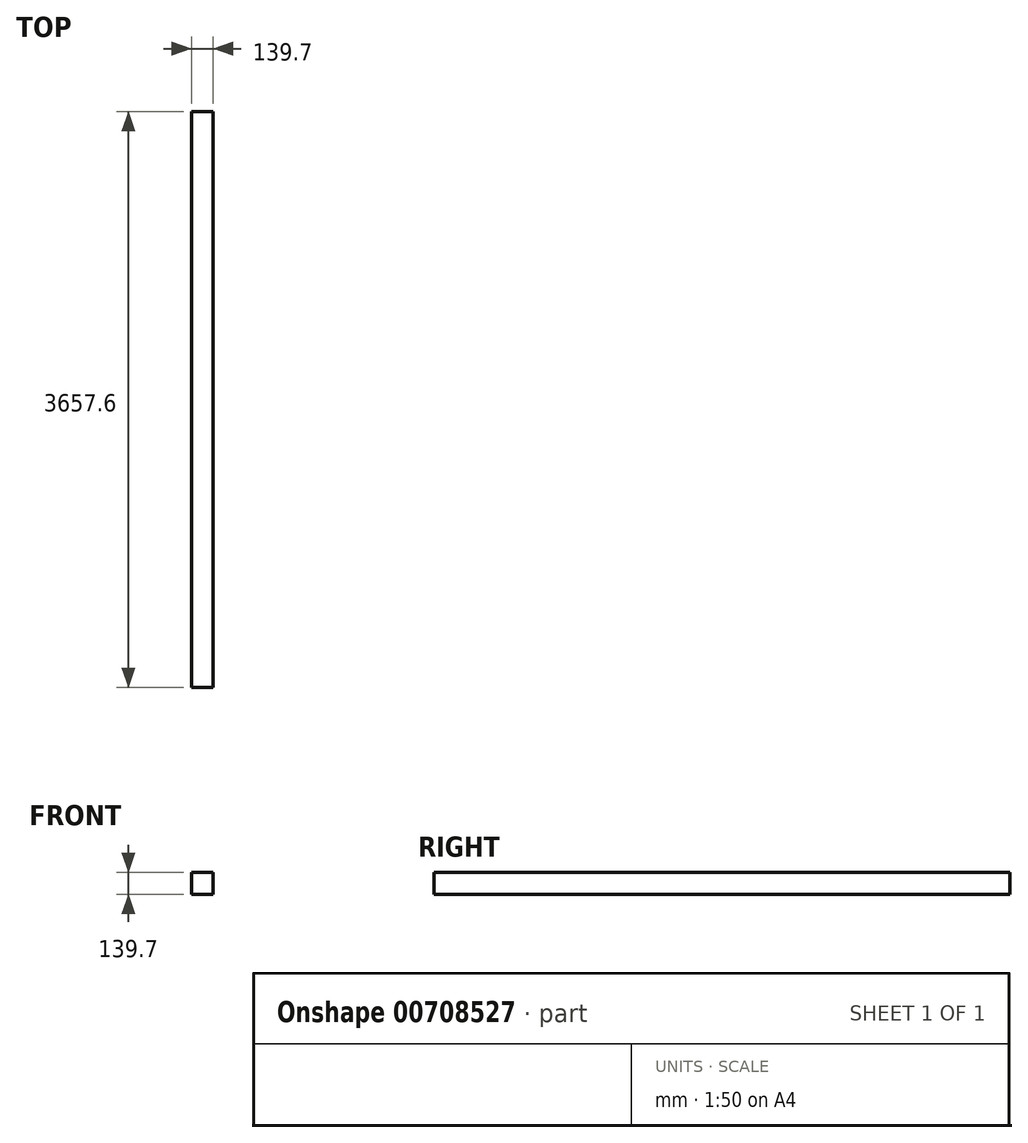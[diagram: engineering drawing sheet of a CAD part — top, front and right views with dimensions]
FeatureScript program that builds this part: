
annotation { "Feature Type Name" : "Feature", "Feature Type Description" : "" }
export const myFeature = defineFeature(function(context is Context, id is Id, definition is map)
    precondition{}
    {
        {
            var Q0;
            Q0=qCreatedBy(makeId("Front.planeOp"),FACE);
            var sketch = newSketch(context, id + "F0", { "sketchPlane" : qUnion([Q0])});
            skLineSegment(sketch, "E0.bottom", {"start": v(-113.25, 94.63) * mm, "end": v(26.45, 94.63) * mm});
            skLineSegment(sketch, "E0.top", {"start": v(-113.25, -45.07) * mm, "end": v(26.45, -45.07) * mm});
            skLineSegment(sketch, "E0.left", {"start": v(-113.25, 94.63) * mm, "end": v(-113.25, -45.07) * mm});
            skLineSegment(sketch, "E0.right", {"start": v(26.45, 94.63) * mm, "end": v(26.45, -45.07) * mm});
            skSolve(sketch);
        }
        {
            var Q0;
            Q0 = qSketchRegion(id + "F0", true);
            extrude(context, id + "F1", {"entities" : qUnion([Q0]), "depth" : 3657.6 * mm, "offsetDistance" : 25.4 * mm});
        }
    });
